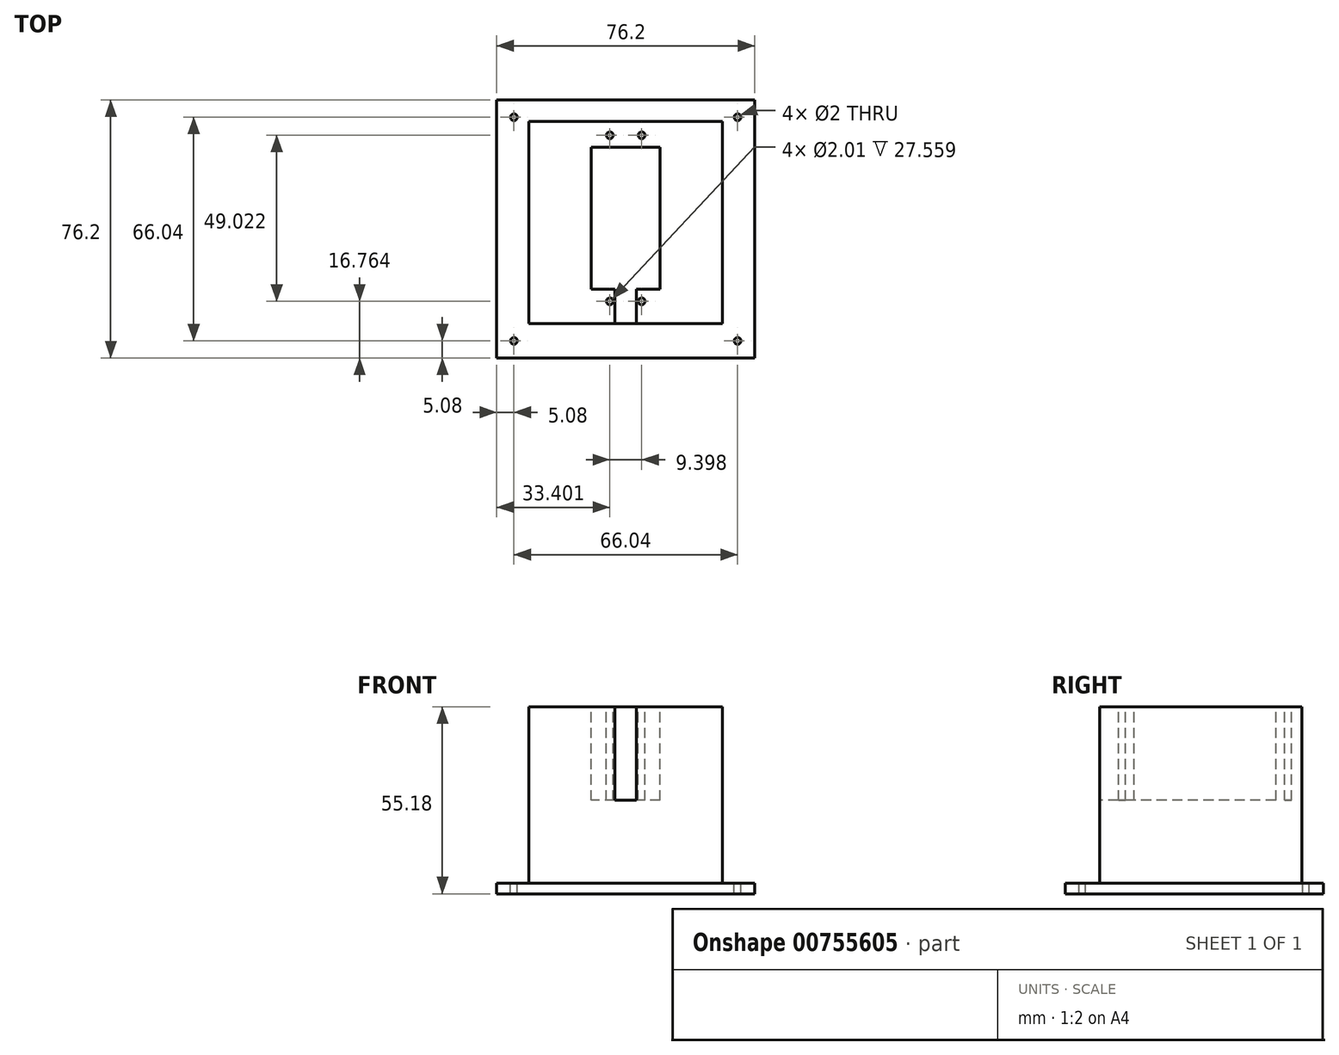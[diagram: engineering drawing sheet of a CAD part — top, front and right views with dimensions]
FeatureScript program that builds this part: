
annotation { "Feature Type Name" : "Feature", "Feature Type Description" : "" }
export const myFeature = defineFeature(function(context is Context, id is Id, definition is map)
    precondition{}
    {
        {
            var Q0;
            Q0=qCreatedBy(makeId("Top.planeOp"),FACE);
            var sketch = newSketch(context, id + "F0", { "sketchPlane" : qUnion([Q0])});
            skLineSegment(sketch, "E0.bottom", {"start": v(38.1, 38.1) * mm, "end": v(-38.1, 38.1) * mm});
            skLineSegment(sketch, "E0.top", {"start": v(38.1, -38.1) * mm, "end": v(-38.1, -38.1) * mm});
            skLineSegment(sketch, "E0.left", {"start": v(38.1, 38.1) * mm, "end": v(38.1, -38.1) * mm});
            skLineSegment(sketch, "E0.right", {"start": v(-38.1, 38.1) * mm, "end": v(-38.1, -38.1) * mm});
            skPoint(sketch, "E0.middle", {"position": v(0, 0) * mm});
            skSolve(sketch);
        }
        {
            var Q0;
            Q0 = qSketchRegion(id + "F0", true);
            extrude(context, id + "F1", {"entities" : qUnion([Q0]), "depth" : 3.17 * mm, "offsetDistance" : 25.4 * mm});
        }
        {
            var Q0;
            Q0=makeQuery(id+"F1.opExtrude","CAP_FACE",FACE,{"disambiguationData":[OSD([sQuery(id+"F0.wireOp",EDGE,"E0.bottom"),sQuery(id+"F0.wireOp",EDGE,"E0.top"),sQuery(id+"F0.wireOp",EDGE,"E0.left"),sQuery(id+"F0.wireOp",EDGE,"E0.right")])],"isStart":false});
            var sketch = newSketch(context, id + "F2", { "sketchPlane" : qUnion([Q0])});
            skLineSegment(sketch, "E1.bottom", {"start": v(33.02, 33.02) * mm, "end": v(-33.02, 33.02) * mm, "construction": true});
            skLineSegment(sketch, "E1.top", {"start": v(33.02, -33.02) * mm, "end": v(-33.02, -33.02) * mm, "construction": true});
            skLineSegment(sketch, "E1.left", {"start": v(33.02, 33.02) * mm, "end": v(33.02, -33.02) * mm, "construction": true});
            skLineSegment(sketch, "E1.right", {"start": v(-33.02, 33.02) * mm, "end": v(-33.02, -33.02) * mm, "construction": true});
            skPoint(sketch, "E1.middle", {"position": v(0, 0) * mm});
            skCircle(sketch, "E2", {"center": v(-33.02, 33.02) * mm, "radius": 1 * mm});
            skCircle(sketch, "E3", {"center": v(-33.02, -33.02) * mm, "radius": 1 * mm});
            skCircle(sketch, "E4", {"center": v(33.02, 33.02) * mm, "radius": 1 * mm});
            skCircle(sketch, "E5", {"center": v(33.02, -33.02) * mm, "radius": 1 * mm});
            skSolve(sketch);
        }
        {
            var Q0;
            Q0 = qSketchRegion(id + "F2", true);
            extrude(context, id + "F3", {"entities" : qUnion([Q0]), "operationType" : NewBodyOperationType.REMOVE, "oppositeDirection" : true, "depth" : 25.4 * mm, "offsetDistance" : 25.4 * mm});
        }
        {
            var Q0;
            Q0=makeQuery(id+"F1.opExtrude","CAP_FACE",FACE,{"disambiguationData":[OSD([sQuery(id+"F0.wireOp",EDGE,"E0.bottom"),sQuery(id+"F0.wireOp",EDGE,"E0.top"),sQuery(id+"F0.wireOp",EDGE,"E0.left"),sQuery(id+"F0.wireOp",EDGE,"E0.right")])],"isStart":false});
            var sketch = newSketch(context, id + "F4", { "sketchPlane" : qUnion([Q0])});
            skLineSegment(sketch, "E6", {"start": v(-28.58, 0) * mm, "end": v(28.58, 0) * mm, "construction": true});
            skLineSegment(sketch, "E7", {"start": v(0, 31.75) * mm, "end": v(0, -27.94) * mm, "construction": true});
            skLineSegment(sketch, "E8.bottom", {"start": v(-28.58, 31.75) * mm, "end": v(28.57, 31.75) * mm});
            skLineSegment(sketch, "E8.top", {"start": v(-28.57, -27.94) * mm, "end": v(28.57, -27.94) * mm});
            skLineSegment(sketch, "E8.left", {"start": v(-28.58, 31.75) * mm, "end": v(-28.58, -27.94) * mm});
            skLineSegment(sketch, "E8.right", {"start": v(28.58, 31.75) * mm, "end": v(28.58, -27.94) * mm});
            skSolve(sketch);
        }
        {
            var Q0;
            Q0 = qSketchRegion(id + "F4", true);
            extrude(context, id + "F5", {"entities" : qUnion([Q0]), "operationType" : NewBodyOperationType.ADD, "depth" : 52 * mm, "offsetDistance" : 25.4 * mm});
        }
        {
            var Q0;
            Q0=makeQuery(id+"F5.opExtrude","CAP_FACE",FACE,{"disambiguationData":[OSD([sQuery(id+"F4.wireOp",EDGE,"E8.bottom"),sQuery(id+"F4.wireOp",EDGE,"E8.top"),sQuery(id+"F4.wireOp",EDGE,"E8.left"),sQuery(id+"F4.wireOp",EDGE,"E8.right")])],"isStart":false});
            var sketch = newSketch(context, id + "F6", { "sketchPlane" : qUnion([Q0])});
            skPoint(sketch, "E9", {"position": v(0, 3.18) * mm});
            skLineSegment(sketch, "E10.bottom", {"start": v(10.16, 24.13) * mm, "end": v(-10.16, 24.13) * mm});
            skLineSegment(sketch, "E10.top", {"start": v(10.16, -17.78) * mm, "end": v(3.17, -17.78) * mm});
            skLineSegment(sketch, "E10.left", {"start": v(10.16, 24.13) * mm, "end": v(10.16, -17.78) * mm});
            skLineSegment(sketch, "E10.right", {"start": v(-10.16, 24.13) * mm, "end": v(-10.16, -17.78) * mm});
            skLineSegment(sketch, "E11", {"start": v(-3.18, -17.78) * mm, "end": v(-3.18, -27.94) * mm});
            skLineSegment(sketch, "E12", {"start": v(3.18, -17.78) * mm, "end": v(3.18, -27.94) * mm});
            skLineSegment(sketch, "E13.trimOffspring", {"start": v(-3.17, -17.78) * mm, "end": v(-10.16, -17.78) * mm});
            skLineSegment(sketch, "E14", {"start": v(-3.18, -27.94) * mm, "end": v(3.18, -27.94) * mm});
            skLineSegment(sketch, "E15", {"start": v(-4.7, 31.75) * mm, "end": v(-4.7, -27.94) * mm, "construction": true});
            skLineSegment(sketch, "E16", {"start": v(4.7, -27.94) * mm, "end": v(4.7, 31.75) * mm, "construction": true});
            skCircle(sketch, "E17", {"center": v(-4.7, 27.69) * mm, "radius": 1 * mm});
            skCircle(sketch, "E18", {"center": v(4.7, 27.69) * mm, "radius": 1 * mm});
            skCircle(sketch, "E19", {"center": v(-4.7, -21.34) * mm, "radius": 1 * mm});
            skCircle(sketch, "E20", {"center": v(4.7, -21.34) * mm, "radius": 1 * mm});
            skSolve(sketch);
        }
        {
            var Q0;
            Q0 = qSketchRegion(id + "F6", true);
            extrude(context, id + "F7", {"entities" : qUnion([Q0]), "operationType" : NewBodyOperationType.REMOVE, "oppositeDirection" : true, "depth" : 27.56 * mm, "offsetDistance" : 25.4 * mm});
        }
    });
